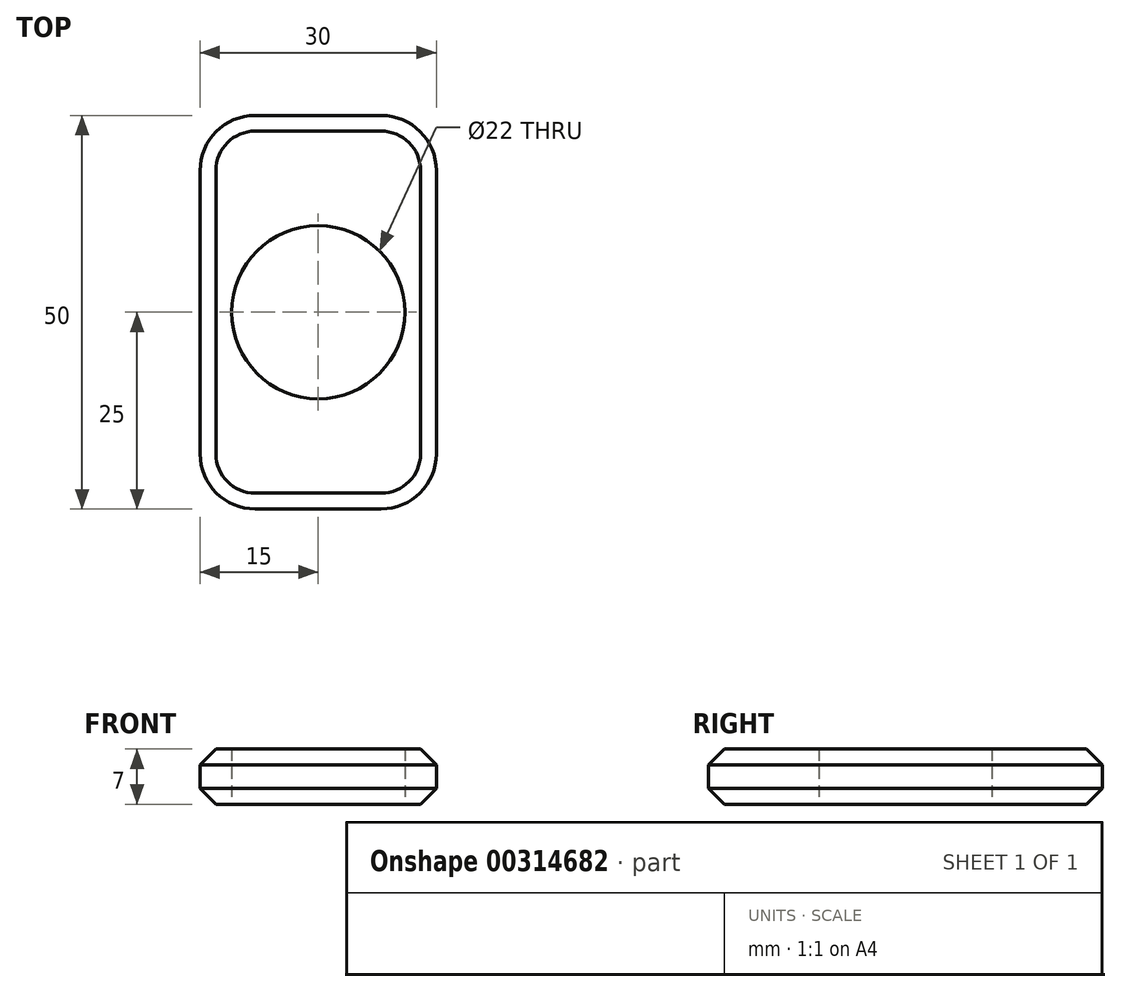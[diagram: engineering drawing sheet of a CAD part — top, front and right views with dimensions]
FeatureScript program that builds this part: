
annotation { "Feature Type Name" : "Feature", "Feature Type Description" : "" }
export const myFeature = defineFeature(function(context is Context, id is Id, definition is map)
    precondition{}
    {
        {
            var Q0;
            Q0=qCreatedBy(makeId("Top.planeOp"),FACE);
            var sketch = newSketch(context, id + "F0", { "sketchPlane" : qUnion([Q0])});
            skCircle(sketch, "E0", {"center": v(0, 0) * mm, "radius": 11 * mm});
            skLineSegment(sketch, "E1.bottom", {"start": v(15, -25) * mm, "end": v(-15, -25) * mm});
            skLineSegment(sketch, "E1.top", {"start": v(15, 25) * mm, "end": v(-15, 25) * mm});
            skLineSegment(sketch, "E1.left", {"start": v(15, -25) * mm, "end": v(15, 25) * mm});
            skLineSegment(sketch, "E1.right", {"start": v(-15, -25) * mm, "end": v(-15, 25) * mm});
            skSolve(sketch);
        }
        {
            var Q0;
            Q0=makeQuery(id+"F0.imprint","IMPRINT",FACE,{"disambiguationData":[TD([[makeQuery(id+"F0.imprint","IMPRINT",EDGE,{"derivedFrom":sQuery(id+"F0.wireOp",EDGE,"E0")}),-1.0]])]});
            extrude(context, id + "F1", {"entities" : qUnion([Q0]), "depth" : 7 * mm, "offsetDistance" : 25 * mm});
        }
        {
            var Q0;
            Q0=makeQuery(id+"F1.opExtrude","SWEPT_EDGE",EDGE,{"disambiguationData":[OSD([sQuery(id+"F0.wireOp",EDGE,"E1.bottom"),sQuery(id+"F0.wireOp",EDGE,"E1.right")])]});
            var Q1;
            Q1=makeQuery(id+"F1.opExtrude","SWEPT_EDGE",EDGE,{"disambiguationData":[OSD([sQuery(id+"F0.wireOp",EDGE,"E1.bottom"),sQuery(id+"F0.wireOp",EDGE,"E1.left")])]});
            var Q2;
            Q2=makeQuery(id+"F1.opExtrude","SWEPT_EDGE",EDGE,{"disambiguationData":[OSD([sQuery(id+"F0.wireOp",EDGE,"E1.top"),sQuery(id+"F0.wireOp",EDGE,"E1.right")])]});
            var Q3;
            Q3=makeQuery(id+"F1.opExtrude","SWEPT_EDGE",EDGE,{"disambiguationData":[OSD([sQuery(id+"F0.wireOp",EDGE,"E1.top"),sQuery(id+"F0.wireOp",EDGE,"E1.left")])]});
            fillet(context, id + "F2", {"entities" : qUnion([Q0, Q1, Q2, Q3]), "radius" : 7 * mm, "tangentPropagation" : true, "allowEdgeOverflow" : false});
        }
        {
            var Q0;
            Q0=makeQuery(id+"F1.opExtrude","CAP_EDGE",EDGE,{"disambiguationData":[OSD([sQuery(id+"F0.wireOp",EDGE,"E1.right")])],"isStart":false});
            var Q1;
            Q1=makeQuery(id+"F1.opExtrude","CAP_EDGE",EDGE,{"disambiguationData":[OSD([sQuery(id+"F0.wireOp",EDGE,"E1.right")])],"isStart":true});
            chamfer(context, id + "F3", {"entities" : qUnion([Q0, Q1]), "width" : 2 * mm, "tangentPropagation" : true});
        }
    });
